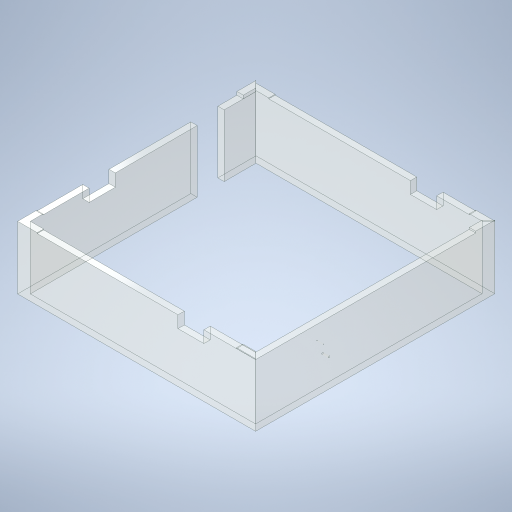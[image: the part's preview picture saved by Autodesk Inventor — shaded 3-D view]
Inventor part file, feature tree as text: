
AUTODESK INVENTOR PART (.ipt)
format: ipt  version: 2024 (Build 280153000, 153)  size: 398,336 bytes
history: native  units: in
note: dims shown in document units (in); Inventor stores cm internally (conversion verified against a paired STEP export)
features: sketch x12, extrude x10, hole x2, plane x1
ambient origin geometry x8: Origin, YZ Plane, XZ Plane, XY Plane, X Axis, Y Axis, Z Axis, Center Point
bodies: Solid1 (feature_tree)
feature tree (25):
  extrude  "Extrusion1"  Depth=0.5in
  extrude  "Extrusion2"  Depth=284.0in
  hole  "Hole1"  [1 undecoded]
  hole  "Hole2"  [1 undecoded]
  extrude  "Extrusion3"  Depth=78.0in
  extrude  "Extrusion5"  Depth=1.0in
  extrude  "Extrusion9"  Depth=1.0in TaperAngle=0.0deg
  extrude  "Extrusion10"  Depth=1.0in TaperAngle=0.0deg
  extrude  "Extrusion11"  Depth=2.0in TaperAngle=0.0deg
  extrude  "Extrusion12"  Depth=1.0in TaperAngle=0.0deg
  extrude  "Extrusion13"  Depth=0.5in
  plane  "Work Plane2"
  extrude  "Extrusion16"  Depth=24.0in
  sketch  "Sketch1"  dims[d1=283.0in d3=0.5in]
  sketch  "Sketch3"  dims[d4=284.0in d5=284.0in]
  sketch  "Sketch4"  dims[d6=8.0in d8=284.0in]
  sketch  "Sketch5"  dims[d9=78.0in d10=0.0in d20=57.0in]
  sketch  "Sketch6"  dims[d25=78.0in d26=0.0in d27=52.375in]
  sketch  "Sketch8"  dims[d28=207.0in]
  sketch  "Sketch13"  dims[d29=0.75in d30=0.75in d31=0.375in d32=0.25in d33=0.5635in d34=1.0in d35=0.8108in d36=35.0in]
  sketch  "Sketch14"  dims[d37=200.0in]
  sketch  "Sketch15"  dims[d38=2.0in d39=0.75in d40=0.375in d41=0.25in d42=0.5635in d43=1.0in d44=0.8108in d49=1.0in d50=0.0in]
  sketch  "Sketch16"  dims[d56=107.0in d60=1.0in d61=0.0in]
  sketch  "Sketch17"  dims[d84=24.0in d85=2.0in d86=0.0in]
  sketch  "Sketch20"  dims[d87=24.0in d88=1.0in d89=0.0in d91=24.6904in d92=24.0in d93=1.0in d94=0.0in d95=24.0in d96=4.0in d97=0.0in d98=24.0in d99=24.0in d100=1.0in d101=0.0in d102=32.5in d103=16.0in d104=1.0in d105=16.0in d106=57.0in d107=33.0in d108=1.0in d118=62.5in d119=19.0in d120=33.0in d121=90.0deg d122=40.0in d123=79.0in d124=34.0in d125=1.0in d126=0.0in d21=0.0344in d22=0.5in d23=0.0344in]
note: 2 required parameter values undecoded (feature->parameter linkage not recoverable at this tier; creation-order binding heuristic only, values carry confidence <= 0.55)
